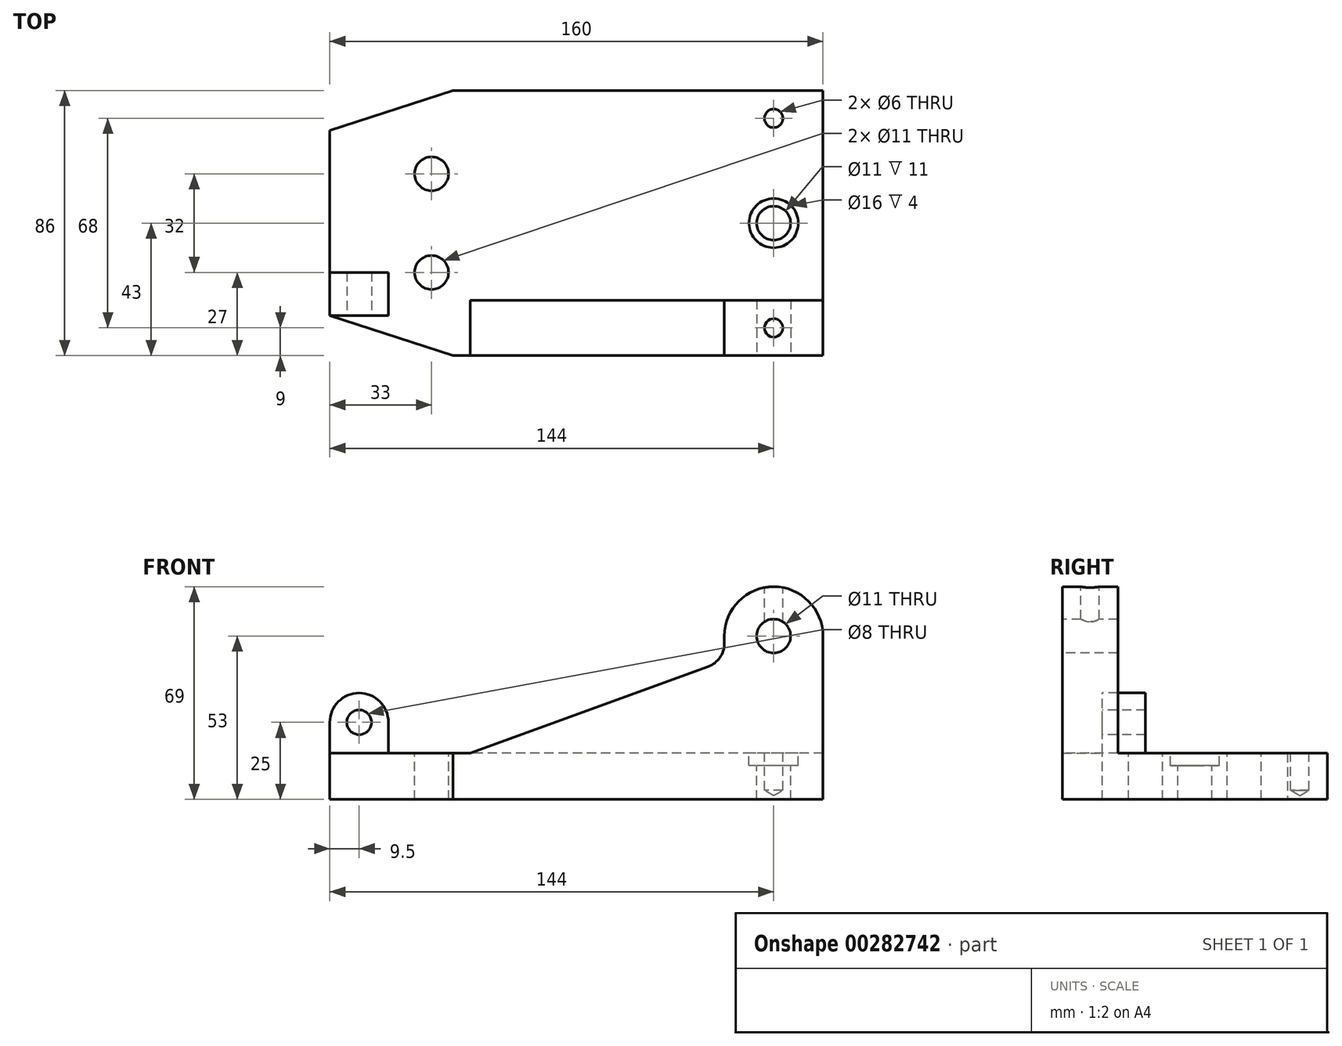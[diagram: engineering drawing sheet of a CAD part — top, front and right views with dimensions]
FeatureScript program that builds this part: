
annotation { "Feature Type Name" : "Feature", "Feature Type Description" : "" }
export const myFeature = defineFeature(function(context is Context, id is Id, definition is map)
    precondition{}
    {
        {
            var Q0;
            Q0=qCreatedBy(makeId("Top.planeOp"),FACE);
            var sketch = newSketch(context, id + "F0", { "sketchPlane" : qUnion([Q0])});
            skLineSegment(sketch, "E0.bottom", {"start": v(80, -43) * mm, "end": v(-80, -43) * mm});
            skLineSegment(sketch, "E0.top", {"start": v(80, 43) * mm, "end": v(-80, 43) * mm});
            skLineSegment(sketch, "E0.left", {"start": v(80, -43) * mm, "end": v(80, 43) * mm});
            skLineSegment(sketch, "E0.right", {"start": v(-80, -43) * mm, "end": v(-80, 43) * mm});
            skPoint(sketch, "E0.middle", {"position": v(0, 0) * mm});
            skSolve(sketch);
        }
        {
            var Q0;
            Q0 = qSketchRegion(id + "F0", true);
            extrude(context, id + "F1", {"entities" : qUnion([Q0]), "depth" : 15 * mm});
        }
        {
            var Q0;
            Q0=makeQuery(id+"F1.opExtrude","SWEPT_FACE",FACE,{"disambiguationData":[OSD([sQuery(id+"F0.wireOp",EDGE,"E0.bottom")])]});
            var sketch = newSketch(context, id + "F2", { "sketchPlane" : qUnion([Q0])});
            skLineSegment(sketch, "E1.0", {"start": v(80, 15) * mm, "end": v(-80, 15) * mm, "construction": true});
            skLineSegment(sketch, "E2.0", {"start": v(80, 0) * mm, "end": v(-80, 0) * mm, "construction": true});
            skLineSegment(sketch, "E3.0", {"start": v(80, 15) * mm, "end": v(80, 0) * mm, "construction": true});
            skLineSegment(sketch, "E4", {"start": v(-34.42, 15) * mm, "end": v(48, 45) * mm});
            skLineSegment(sketch, "E5", {"start": v(48, 45) * mm, "end": v(48, 53) * mm});
            skArc(sketch, "E6", {"start": v(80, 53) * mm, "mid": v(64, 69) * mm, "end": v(48, 53) * mm});
            skLineSegment(sketch, "E7", {"start": v(80, 53) * mm, "end": v(80, 15) * mm});
            skLineSegment(sketch, "E8", {"start": v(-34.42, 15) * mm, "end": v(80, 15) * mm});
            skSolve(sketch);
        }
        {
            var Q0;
            Q0 = qSketchRegion(id + "F2", true);
            extrude(context, id + "F3", {"entities" : qUnion([Q0]), "operationType" : NewBodyOperationType.ADD, "oppositeDirection" : true, "depth" : 18 * mm});
        }
        {
            var Q0;
            Q0=makeQuery(id+"F3.opExtrude","SWEPT_EDGE",EDGE,{"disambiguationData":[OSD([sQuery(id+"F2.wireOp",EDGE,"E4"),sQuery(id+"F2.wireOp",EDGE,"E5")])]});
            fillet(context, id + "F4", {"entities" : qUnion([Q0]), "radius" : 8 * mm, "tangentPropagation" : true, "allowEdgeOverflow" : false});
        }
        {
            var Q0;
            Q0=makeQuery(id+"F3.boolean.opBoolean","MERGE",FACE,{"derivedFrom":[makeQuery(id+"F1.opExtrude","SWEPT_FACE",FACE,{"disambiguationData":[OSD([sQuery(id+"F0.wireOp",EDGE,"E0.bottom")])]}),makeQuery(id+"F3.opExtrude","CAP_FACE",FACE,{"disambiguationData":[OSD([sQuery(id+"F2.wireOp",EDGE,"E4"),sQuery(id+"F2.wireOp",EDGE,"E5"),sQuery(id+"F2.wireOp",EDGE,"E6"),sQuery(id+"F2.wireOp",EDGE,"E7"),sQuery(id+"F2.wireOp",EDGE,"E8")])],"isStart":true})]});
            var sketch = newSketch(context, id + "F5", { "sketchPlane" : qUnion([Q0])});
            skArc(sketch, "E9.0", {"start": v(80, 53) * mm, "mid": v(64, 69) * mm, "end": v(48, 53) * mm, "construction": true});
            skSolve(sketch);
        }
        {
            var Q0;
            Q0=sQuery(id+"F5.wireOp",VERTEX,"E9.0.center");
            var Q1;
            Q1=makeQuery(id+"F1.opExtrude","SWEPT_BODY",BODY,{"disambiguationData":[OSD([sQuery(id+"F0.wireOp",EDGE,"E0.bottom"),sQuery(id+"F0.wireOp",EDGE,"E0.top"),sQuery(id+"F0.wireOp",EDGE,"E0.left"),sQuery(id+"F0.wireOp",EDGE,"E0.right")])]});
            hole(context, id + "F6", {"style" : HoleStyle.SIMPLE, "endStyle" : HoleEndStyle.THROUGH, "holeDiameter" : 11 * mm, "tappedDepth" : 12 * mm, "tapClearance" : 3, "locations" : qUnion([Q0]), "scope" : qUnion([Q1])});
        }
        {
            var Q0;
            Q0=qCreatedBy(makeId("Front.planeOp"),FACE);
            cPlane(context, id + "F7", {"entities" : qUnion([Q0]), "cplaneType" : CPlaneType.OFFSET, "offset" : 30 * mm, "width" : 150 * mm, "height" : 150 * mm});
        }
        {
            var Q0;
            Q0=qCreatedBy(id+"F7.planeOp",FACE);
            var sketch = newSketch(context, id + "F8", { "sketchPlane" : qUnion([Q0])});
            skLineSegment(sketch, "E10.0", {"start": v(-34.42, 15) * mm, "end": v(-80, 15) * mm, "construction": true});
            skLineSegment(sketch, "E11", {"start": v(-80, 15) * mm, "end": v(-80, 25) * mm});
            skArc(sketch, "E12", {"start": v(-61, 25) * mm, "mid": v(-70.5, 34.5) * mm, "end": v(-80, 25) * mm});
            skLineSegment(sketch, "E13", {"start": v(-61, 25) * mm, "end": v(-61, 15) * mm});
            skLineSegment(sketch, "E14", {"start": v(-61, 15) * mm, "end": v(-80, 15) * mm});
            skSolve(sketch);
        }
        {
            var Q0;
            Q0 = qSketchRegion(id + "F8", true);
            extrude(context, id + "F9", {"entities" : qUnion([Q0]), "operationType" : NewBodyOperationType.ADD, "oppositeDirection" : true, "depth" : 14 * mm});
        }
        {
            var Q0;
            Q0=makeQuery(id+"F9.opExtrude","CAP_FACE",FACE,{"disambiguationData":[OSD([sQuery(id+"F8.wireOp",EDGE,"E11"),sQuery(id+"F8.wireOp",EDGE,"E12"),sQuery(id+"F8.wireOp",EDGE,"E13"),sQuery(id+"F8.wireOp",EDGE,"E14")])],"isStart":true});
            var sketch = newSketch(context, id + "F10", { "sketchPlane" : qUnion([Q0])});
            skArc(sketch, "E15.0", {"start": v(-61, 25) * mm, "mid": v(-70.5, 34.5) * mm, "end": v(-80, 25) * mm, "construction": true});
            skSolve(sketch);
        }
        {
            var Q0;
            Q0=sQuery(id+"F10.wireOp",VERTEX,"E15.0.center");
            var Q1;
            Q1=makeQuery(id+"F1.opExtrude","SWEPT_BODY",BODY,{"disambiguationData":[OSD([sQuery(id+"F0.wireOp",EDGE,"E0.bottom"),sQuery(id+"F0.wireOp",EDGE,"E0.top"),sQuery(id+"F0.wireOp",EDGE,"E0.left"),sQuery(id+"F0.wireOp",EDGE,"E0.right")])]});
            hole(context, id + "F11", {"style" : HoleStyle.SIMPLE, "endStyle" : HoleEndStyle.THROUGH, "holeDiameter" : 8 * mm, "tappedDepth" : 12 * mm, "tapClearance" : 3, "locations" : qUnion([Q0]), "scope" : qUnion([Q1])});
        }
        {
            var Q0;
            Q0=makeQuery(id+"F1.opExtrude","SWEPT_EDGE",EDGE,{"disambiguationData":[OSD([sQuery(id+"F0.wireOp",EDGE,"E0.bottom"),sQuery(id+"F0.wireOp",EDGE,"E0.right")])]});
            chamfer(context, id + "F12", {"entities" : qUnion([Q0]), "chamferType" : ChamferType.TWO_OFFSETS, "width1" : 40 * mm, "oppositeDirection" : false, "width2" : 13 * mm, "tangentPropagation" : true});
        }
        {
            var Q0;
            Q0=makeQuery(id+"F1.opExtrude","SWEPT_EDGE",EDGE,{"disambiguationData":[OSD([sQuery(id+"F0.wireOp",EDGE,"E0.top"),sQuery(id+"F0.wireOp",EDGE,"E0.right")])]});
            chamfer(context, id + "F13", {"entities" : qUnion([Q0]), "chamferType" : ChamferType.TWO_OFFSETS, "width1" : 13 * mm, "oppositeDirection" : false, "width2" : 40 * mm, "tangentPropagation" : true});
        }
        {
            var Q0;
            Q0=makeQuery(id+"F1.opExtrude","CAP_FACE",FACE,{"disambiguationData":[OSD([sQuery(id+"F0.wireOp",EDGE,"E0.bottom"),sQuery(id+"F0.wireOp",EDGE,"E0.top"),sQuery(id+"F0.wireOp",EDGE,"E0.left"),sQuery(id+"F0.wireOp",EDGE,"E0.right")])],"isStart":false});
            cPlane(context, id + "F14", {"entities" : qUnion([Q0]), "cplaneType" : CPlaneType.OFFSET, "offset" : 54 * mm, "width" : 150 * mm, "height" : 150 * mm});
        }
        {
            var Q0;
            Q0=qCreatedBy(id+"F14.planeOp",FACE);
            var sketch = newSketch(context, id + "F15", { "sketchPlane" : qUnion([Q0])});
            skLineSegment(sketch, "E16.0", {"start": v(80, 43) * mm, "end": v(48, 43) * mm, "construction": true});
            skLineSegment(sketch, "E17.0", {"start": v(80, 25) * mm, "end": v(48, 25) * mm, "construction": true});
            skLineSegment(sketch, "E18.0", {"start": v(80, -25) * mm, "end": v(48, -25) * mm, "construction": true});
            skLineSegment(sketch, "E19.0", {"start": v(80, -43) * mm, "end": v(48, -43) * mm, "construction": true});
            skLineSegment(sketch, "E20", {"start": v(64, 43) * mm, "end": v(64, 25) * mm, "construction": true});
            skLineSegment(sketch, "E21", {"start": v(64, -25) * mm, "end": v(64, -43) * mm, "construction": true});
            skPoint(sketch, "E22", {"position": v(64, 34) * mm});
            skPoint(sketch, "E23", {"position": v(64, -34) * mm});
            skSolve(sketch);
        }
        {
            var Q0;
            Q0=sQuery(id+"F15.wireOp",VERTEX,"E23");
            var Q1;
            Q1=sQuery(id+"F15.wireOp",VERTEX,"E22");
            var Q2;
            Q2=makeQuery(id+"F1.opExtrude","SWEPT_BODY",BODY,{"disambiguationData":[OSD([sQuery(id+"F0.wireOp",EDGE,"E0.bottom"),sQuery(id+"F0.wireOp",EDGE,"E0.top"),sQuery(id+"F0.wireOp",EDGE,"E0.left"),sQuery(id+"F0.wireOp",EDGE,"E0.right")])]});
            hole(context, id + "F16", {"style" : HoleStyle.SIMPLE, "endStyle" : HoleEndStyle.BLIND, "holeDiameter" : 6 * mm, "holeDepth" : 12 * mm, "tappedDepth" : 12 * mm, "tapClearance" : 3, "locations" : qUnion([Q0, Q1]), "scope" : qUnion([Q2])});
        }
        {
            var Q0;
            Q0=makeQuery(id+"F1.opExtrude","CAP_FACE",FACE,{"disambiguationData":[OSD([sQuery(id+"F0.wireOp",EDGE,"E0.bottom"),sQuery(id+"F0.wireOp",EDGE,"E0.top"),sQuery(id+"F0.wireOp",EDGE,"E0.left"),sQuery(id+"F0.wireOp",EDGE,"E0.right")])],"isStart":false});
            var sketch = newSketch(context, id + "F17", { "sketchPlane" : qUnion([Q0])});
            skLineSegment(sketch, "E24.0", {"start": v(-80, -16) * mm, "end": v(-80, 16) * mm, "construction": true});
            skLineSegment(sketch, "E25", {"start": v(-80, 0) * mm, "end": v(80, 0) * mm, "construction": true});
            skPoint(sketch, "E26", {"position": v(-47, 16) * mm});
            skPoint(sketch, "E27", {"position": v(-47, -16) * mm});
            skSolve(sketch);
        }
        {
            var Q0;
            Q0=sQuery(id+"F17.wireOp",VERTEX,"E27");
            var Q1;
            Q1=sQuery(id+"F17.wireOp",VERTEX,"E26");
            var Q2;
            Q2=makeQuery(id+"F1.opExtrude","SWEPT_BODY",BODY,{"disambiguationData":[OSD([sQuery(id+"F0.wireOp",EDGE,"E0.bottom"),sQuery(id+"F0.wireOp",EDGE,"E0.top"),sQuery(id+"F0.wireOp",EDGE,"E0.left"),sQuery(id+"F0.wireOp",EDGE,"E0.right")])]});
            hole(context, id + "F18", {"style" : HoleStyle.SIMPLE, "endStyle" : HoleEndStyle.THROUGH, "holeDiameter" : 11 * mm, "tappedDepth" : 12 * mm, "tapClearance" : 3, "locations" : qUnion([Q0, Q1]), "scope" : qUnion([Q2])});
        }
        {
            var Q0;
            Q0=makeQuery(id+"F1.opExtrude","CAP_FACE",FACE,{"disambiguationData":[OSD([sQuery(id+"F0.wireOp",EDGE,"E0.bottom"),sQuery(id+"F0.wireOp",EDGE,"E0.top"),sQuery(id+"F0.wireOp",EDGE,"E0.left"),sQuery(id+"F0.wireOp",EDGE,"E0.right")])],"isStart":false});
            var sketch = newSketch(context, id + "F19", { "sketchPlane" : qUnion([Q0])});
            skLineSegment(sketch, "E28.0", {"start": v(80, -25) * mm, "end": v(80, 25) * mm, "construction": true});
            skLineSegment(sketch, "E29", {"start": v(80, 0) * mm, "end": v(64, 0) * mm, "construction": true});
            skPoint(sketch, "E29.endSnap0", {"position": v(80, 0) * mm});
            skPoint(sketch, "E30", {"position": v(64, 0) * mm});
            skSolve(sketch);
        }
        {
            var Q0;
            Q0=sQuery(id+"F19.wireOp",VERTEX,"E30");
            var Q1;
            Q1=makeQuery(id+"F1.opExtrude","SWEPT_BODY",BODY,{"disambiguationData":[OSD([sQuery(id+"F0.wireOp",EDGE,"E0.bottom"),sQuery(id+"F0.wireOp",EDGE,"E0.top"),sQuery(id+"F0.wireOp",EDGE,"E0.left"),sQuery(id+"F0.wireOp",EDGE,"E0.right")])]});
            hole(context, id + "F20", {"style" : HoleStyle.C_BORE, "endStyle" : HoleEndStyle.THROUGH, "holeDiameter" : 11 * mm, "cBoreDiameter" : 16 * mm, "cBoreDepth" : 4 * mm, "tappedDepth" : 12 * mm, "tapClearance" : 3, "locations" : qUnion([Q0]), "scope" : qUnion([Q1])});
        }
    });
